# Revit family: NC2011005
name_source: partatom
category: Plumbing Fixtures
revit_build: Autodesk Revit 2016 (Build: 20150220_1215(x64)
units: mm (PartAtom-declared; Revit-internal decimal feet)

## family parameters
Always vertical = Yes
Cut with Voids When Loaded = No
Host = Wall
OmniClass Number = 23.45.00.00
OmniClass Title = Sanitary, Laundry, and Cleaning Equipment
Part Type = Normal
Room Calculation Point = No
Round Connector Dimension = Use Diameter
Shared = No

## types (1)
- 355 x 600 x 400
    Assembly Code = D2010110
    CW Connection = Yes
    Depth = 600 mm
    Description = Inodoro elongado de acero inoxidable tipo AISI 304
diseñado especialmente para condiciones de vandalismo
extremo; todas las piezas interiores, incluyendo lass tuberías
están completamente soldadas. Todas las superficies
expuestas de acero inoxidable tiene una terminación
pulido satinado. El artefacto puede soportar hasta 1.500 kg
de carga.
Este WC es de alimentacion vertical para funcionamiento
con fluxor recto expuesto y descarga vertical al muro.
    HW Connection = No
    Height = 400 mm  [stored 1.31234 ft]
    Manufacturer = CHC
    Material = Stainless Steel, Brushed
    Model = NC2011005
    Type Image = NC2011005.jpg
    URL = www.grupochc.cl
    Vent Connection = No
    Waste Connection = Yes
    Waste Height = 220 mm
    Width = 355 mm

note: [stored X ft] marks values corroborated as IEEE doubles in the binary element streams (Revit-internal decimal feet)

## geometry (parser evidence)
native form markers: Blend x4, Sweep x2
no freeform markers — native parametric forms only
